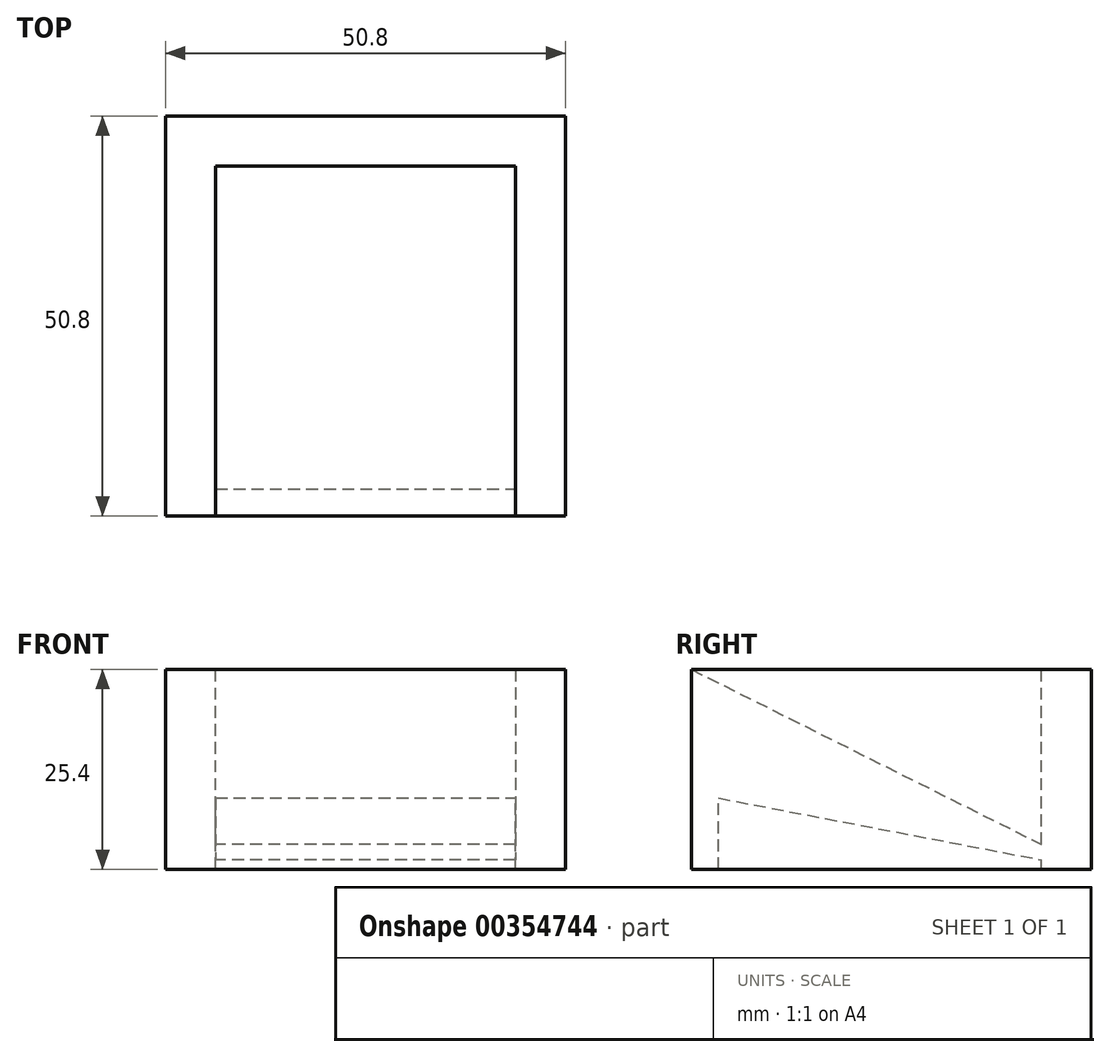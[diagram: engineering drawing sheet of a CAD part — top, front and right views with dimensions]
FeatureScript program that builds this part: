
annotation { "Feature Type Name" : "Feature", "Feature Type Description" : "" }
export const myFeature = defineFeature(function(context is Context, id is Id, definition is map)
    precondition{}
    {
        {
            var Q0;
            Q0=qCreatedBy(makeId("Top.planeOp"),FACE);
            var sketch = newSketch(context, id + "F0", { "sketchPlane" : qUnion([Q0])});
            skLineSegment(sketch, "E0.bottom", {"start": v(25.4, -25.4) * mm, "end": v(-25.4, -25.4) * mm});
            skLineSegment(sketch, "E0.top", {"start": v(25.4, 25.4) * mm, "end": v(-25.4, 25.4) * mm});
            skLineSegment(sketch, "E0.left", {"start": v(25.4, -25.4) * mm, "end": v(25.4, 25.4) * mm});
            skLineSegment(sketch, "E0.right", {"start": v(-25.4, -25.4) * mm, "end": v(-25.4, 25.4) * mm});
            skPoint(sketch, "E0.middle", {"position": v(0, 0) * mm});
            skSolve(sketch);
        }
        {
            var Q0;
            Q0=makeQuery(id+"F0.imprint","IMPRINT",FACE,{"disambiguationData":[TD([[makeQuery(id+"F0.imprint","IMPRINT",EDGE,{"derivedFrom":sQuery(id+"F0.wireOp",EDGE,"E0.bottom")}),-1.0]])]});
            extrude(context, id + "F1", {"entities" : qUnion([Q0]), "depth" : 25.4 * mm});
        }
        {
            var Q0;
            Q0=makeQuery(id+"F1.opExtrude","CAP_FACE",FACE,{"disambiguationData":[OSD([sQuery(id+"F0.wireOp",EDGE,"E0.bottom"),sQuery(id+"F0.wireOp",EDGE,"E0.top"),sQuery(id+"F0.wireOp",EDGE,"E0.left"),sQuery(id+"F0.wireOp",EDGE,"E0.right")])],"isStart":false});
            var sketch = newSketch(context, id + "F2", { "sketchPlane" : qUnion([Q0])});
            skLineSegment(sketch, "E1.bottom", {"start": v(19.05, -69.85) * mm, "end": v(-19.05, -69.85) * mm});
            skLineSegment(sketch, "E1.top", {"start": v(19.05, 19.05) * mm, "end": v(-19.05, 19.05) * mm});
            skLineSegment(sketch, "E1.left", {"start": v(19.05, -69.85) * mm, "end": v(19.05, 19.05) * mm});
            skLineSegment(sketch, "E1.right", {"start": v(-19.05, -69.85) * mm, "end": v(-19.05, 19.05) * mm});
            skPoint(sketch, "E1.middle", {"position": v(0, -25.4) * mm});
            skSolve(sketch);
        }
        {
            var Q0;
            {var subQ0=sQuery(id+"F2.wireOp",EDGE,"E1.top");Q0=makeQuery(id+"F2.imprint","IMPRINT",FACE,{"disambiguationData":[TD([[makeQuery(id+"F2.imprint","IMPRINT",EDGE,{"derivedFrom":subQ0}),1.0]])]});}
            extrude(context, id + "F3", {"entities" : qUnion([Q0]), "operationType" : NewBodyOperationType.REMOVE, "oppositeDirection" : true, "depth" : 25.4 * mm, "offsetDistance" : 25.4 * mm});
        }
        {
            var Q0;
            Q0=makeQuery(id+"F1.opExtrude","SWEPT_FACE",FACE,{"disambiguationData":[OSD([sQuery(id+"F0.wireOp",EDGE,"E0.left")])]});
            var sketch = newSketch(context, id + "F4", { "sketchPlane" : qUnion([Q0])});
            skLineSegment(sketch, "E2", {"start": v(-25.4, 25.4) * mm, "end": v(25.4, 0) * mm});
            skLineSegment(sketch, "E3", {"start": v(-25.4, 0) * mm, "end": v(-25.4, 25.4) * mm});
            skPoint(sketch, "E4", {"position": v(-21.97, 0) * mm});
            skPoint(sketch, "E5", {"position": v(-22.5, 14.5) * mm});
            skLineSegment(sketch, "E6", {"start": v(-21.97, 0) * mm, "end": v(-21.97, 9.06) * mm});
            skLineSegment(sketch, "E7", {"start": v(-21.97, 9.06) * mm, "end": v(25.4, 0) * mm});
            skSolve(sketch);
        }
        {
            var Q0;
            Q0=makeQuery(id+"F4.imprint","IMPRINT",FACE,{"disambiguationData":[TD([[makeQuery(id+"F4.imprint","IMPRINT",EDGE,{"derivedFrom":sQuery(id+"F4.wireOp",EDGE,"E2")}),-1.0]])]});
            extrude(context, id + "F5", {"entities" : qUnion([Q0]), "operationType" : NewBodyOperationType.ADD, "oppositeDirection" : true, "depth" : 47.75 * mm, "offsetDistance" : 25.4 * mm});
        }
    });
